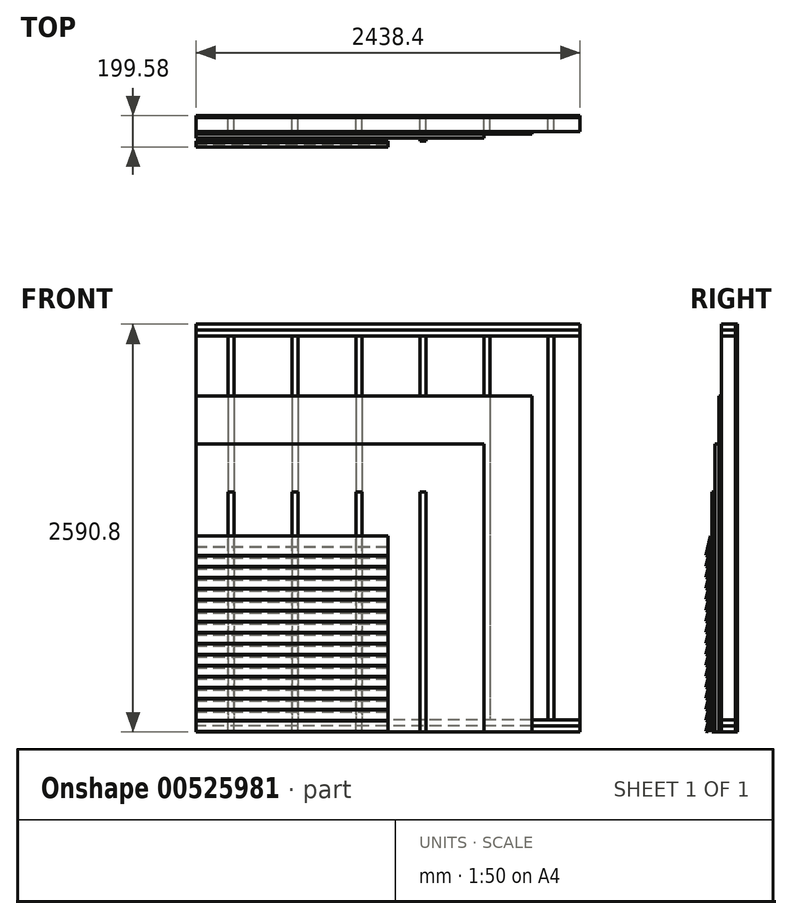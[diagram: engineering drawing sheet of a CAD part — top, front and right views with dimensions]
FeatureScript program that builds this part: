
annotation { "Feature Type Name" : "Feature", "Feature Type Description" : "" }
export const myFeature = defineFeature(function(context is Context, id is Id, definition is map)
    precondition{}
    {
        {
            var Q0;
            Q0=qCreatedBy(makeId("Right.planeOp"),FACE);
            var sketch = newSketch(context, id + "F0", { "sketchPlane" : qUnion([Q0])});
            skLineSegment(sketch, "E0.bottom", {"start": v(44.45, -1219.2) * mm, "end": v(-44.45, -1219.2) * mm});
            skLineSegment(sketch, "E0.top", {"start": v(44.45, -1257.3) * mm, "end": v(-44.45, -1257.3) * mm});
            skLineSegment(sketch, "E0.left", {"start": v(44.45, -1219.2) * mm, "end": v(44.45, -1257.3) * mm});
            skLineSegment(sketch, "E0.right", {"start": v(-44.45, -1219.2) * mm, "end": v(-44.45, -1257.3) * mm});
            skLineSegment(sketch, "E1.top", {"start": v(44.45, -1295.4) * mm, "end": v(-44.45, -1295.4) * mm});
            skLineSegment(sketch, "E1.left", {"start": v(44.45, -1257.3) * mm, "end": v(44.45, -1295.4) * mm});
            skLineSegment(sketch, "E1.right", {"start": v(-44.45, -1257.3) * mm, "end": v(-44.45, -1295.4) * mm});
            skLineSegment(sketch, "E2.bottom", {"start": v(44.45, 1295.4) * mm, "end": v(-44.45, 1295.4) * mm});
            skLineSegment(sketch, "E2.top", {"start": v(44.45, 1257.3) * mm, "end": v(-44.45, 1257.3) * mm});
            skLineSegment(sketch, "E2.left", {"start": v(44.45, 1295.4) * mm, "end": v(44.45, 1257.3) * mm});
            skLineSegment(sketch, "E2.right", {"start": v(-44.45, 1295.4) * mm, "end": v(-44.45, 1257.3) * mm});
            skLineSegment(sketch, "E3.top", {"start": v(44.45, 1219.2) * mm, "end": v(-44.45, 1219.2) * mm});
            skLineSegment(sketch, "E3.left", {"start": v(44.45, 1257.3) * mm, "end": v(44.45, 1219.2) * mm});
            skLineSegment(sketch, "E3.right", {"start": v(-44.45, 1257.3) * mm, "end": v(-44.45, 1219.2) * mm});
            skLineSegment(sketch, "E4", {"start": v(0, 0) * mm, "end": v(0, 1219.2) * mm, "construction": true});
            skLineSegment(sketch, "E5", {"start": v(0, 0) * mm, "end": v(0, -1219.2) * mm, "construction": true});
            skSolve(sketch);
        }
        {
            var Q0;
            Q0=makeQuery(id+"F0.imprint","IMPRINT",FACE,{"disambiguationData":[TD([[makeQuery(id+"F0.imprint","IMPRINT",EDGE,{"derivedFrom":sQuery(id+"F0.wireOp",EDGE,"E0.top")}),1.0]])]});
            var Q1;
            Q1=makeQuery(id+"F0.imprint","IMPRINT",FACE,{"disambiguationData":[TD([[makeQuery(id+"F0.imprint","IMPRINT",EDGE,{"derivedFrom":sQuery(id+"F0.wireOp",EDGE,"E2.bottom")}),1.0]])]});
            extrude(context, id + "F1", {"entities" : qUnion([Q0, Q1]), "endBound" : BoundingType.SYMMETRIC, "depth" : 2438.4 * mm, "offsetDistance" : 25.4 * mm});
        }
        {
            var Q0;
            Q0=makeQuery(id+"F0.imprint","IMPRINT",FACE,{"disambiguationData":[TD([[makeQuery(id+"F0.imprint","IMPRINT",EDGE,{"derivedFrom":sQuery(id+"F0.wireOp",EDGE,"E2.top")}),1.0]])]});
            var Q1;
            Q1=makeQuery(id+"F0.imprint","IMPRINT",FACE,{"disambiguationData":[TD([[makeQuery(id+"F0.imprint","IMPRINT",EDGE,{"derivedFrom":sQuery(id+"F0.wireOp",EDGE,"E0.bottom")}),1.0]])]});
            extrude(context, id + "F2", {"entities" : qUnion([Q0, Q1]), "endBound" : BoundingType.SYMMETRIC, "depth" : 2438.4 * mm, "offsetDistance" : 25.4 * mm});
        }
        {
            var Q0;
            Q0=makeQuery(id+"F2.opExtrude","SWEPT_FACE",FACE,{"disambiguationData":[OSD([sQuery(id+"F0.wireOp",EDGE,"E0.bottom")])]});
            var sketch = newSketch(context, id + "F3", { "sketchPlane" : qUnion([Q0])});
            skLineSegment(sketch, "E6.bottom", {"start": v(-1016, 44.45) * mm, "end": v(-977.9, 44.45) * mm});
            skLineSegment(sketch, "E6.top", {"start": v(-1016, -44.45) * mm, "end": v(-977.9, -44.45) * mm});
            skLineSegment(sketch, "E6.left", {"start": v(-1016, 44.45) * mm, "end": v(-1016, -44.45) * mm});
            skLineSegment(sketch, "E6.right", {"start": v(-977.9, 44.45) * mm, "end": v(-977.9, -44.45) * mm});
            skLineSegment(sketch, "E7.1.0.0", {"start": v(-609.6, 44.45) * mm, "end": v(-571.5, 44.45) * mm});
            skLineSegment(sketch, "E7.1.0.1", {"start": v(-609.6, 44.45) * mm, "end": v(-609.6, -44.45) * mm});
            skLineSegment(sketch, "E7.1.0.2", {"start": v(-571.5, 44.45) * mm, "end": v(-571.5, -44.45) * mm});
            skLineSegment(sketch, "E7.1.0.3", {"start": v(-609.6, -44.45) * mm, "end": v(-571.5, -44.45) * mm});
            skLineSegment(sketch, "E7.2.0.0", {"start": v(-203.2, 44.45) * mm, "end": v(-165.1, 44.45) * mm});
            skLineSegment(sketch, "E7.2.0.1", {"start": v(-203.2, 44.45) * mm, "end": v(-203.2, -44.45) * mm});
            skLineSegment(sketch, "E7.2.0.2", {"start": v(-165.1, 44.45) * mm, "end": v(-165.1, -44.45) * mm});
            skLineSegment(sketch, "E7.2.0.3", {"start": v(-203.2, -44.45) * mm, "end": v(-165.1, -44.45) * mm});
            skLineSegment(sketch, "E7.3.0.0", {"start": v(203.2, 44.45) * mm, "end": v(241.3, 44.45) * mm});
            skLineSegment(sketch, "E7.3.0.1", {"start": v(203.2, 44.45) * mm, "end": v(203.2, -44.45) * mm});
            skLineSegment(sketch, "E7.3.0.2", {"start": v(241.3, 44.45) * mm, "end": v(241.3, -44.45) * mm});
            skLineSegment(sketch, "E7.3.0.3", {"start": v(203.2, -44.45) * mm, "end": v(241.3, -44.45) * mm});
            skLineSegment(sketch, "E7.4.0.0", {"start": v(609.6, 44.45) * mm, "end": v(647.7, 44.45) * mm});
            skLineSegment(sketch, "E7.4.0.1", {"start": v(609.6, 44.45) * mm, "end": v(609.6, -44.45) * mm});
            skLineSegment(sketch, "E7.4.0.2", {"start": v(647.7, 44.45) * mm, "end": v(647.7, -44.45) * mm});
            skLineSegment(sketch, "E7.4.0.3", {"start": v(609.6, -44.45) * mm, "end": v(647.7, -44.45) * mm});
            skLineSegment(sketch, "E7.5.0.0", {"start": v(1016, 44.45) * mm, "end": v(1054.1, 44.45) * mm});
            skLineSegment(sketch, "E7.5.0.1", {"start": v(1016, 44.45) * mm, "end": v(1016, -44.45) * mm});
            skLineSegment(sketch, "E7.5.0.2", {"start": v(1054.1, 44.45) * mm, "end": v(1054.1, -44.45) * mm});
            skLineSegment(sketch, "E7.5.0.3", {"start": v(1016, -44.45) * mm, "end": v(1054.1, -44.45) * mm});
            skLineSegment(sketch, "E7.direction1", {"start": v(-1016, -44.45) * mm, "end": v(-609.6, -44.45) * mm, "construction": true});
            skSolve(sketch);
        }
        {
            var Q0;
            Q0 = qSketchRegion(id + "F3", true);
            var Q1;
            Q1=makeQuery(id+"F2.opExtrude","SWEPT_FACE",FACE,{"disambiguationData":[OSD([sQuery(id+"F0.wireOp",EDGE,"E3.top")])]});
            extrude(context, id + "F4", {"entities" : qUnion([Q0]), "endBound" : BoundingType.UP_TO_SURFACE, "depth" : 25.4 * mm, "endBoundEntityFace" : qUnion([Q1]), "offsetDistance" : 25.4 * mm});
        }
        {
            var Q0;
            Q0=makeQuery(id+"F1.opExtrude","CAP_FACE",FACE,{"disambiguationData":[OSD([sQuery(id+"F0.wireOp",EDGE,"E0.top"),sQuery(id+"F0.wireOp",EDGE,"E1.top"),sQuery(id+"F0.wireOp",EDGE,"E1.left"),sQuery(id+"F0.wireOp",EDGE,"E1.right")])],"isStart":true});
            var sketch = newSketch(context, id + "F5", { "sketchPlane" : qUnion([Q0])});
            skLineSegment(sketch, "E8.bottom", {"start": v(44.45, -1295.4) * mm, "end": v(60.32, -1295.4) * mm});
            skLineSegment(sketch, "E8.top", {"start": v(44.45, 838.2) * mm, "end": v(60.32, 838.2) * mm});
            skLineSegment(sketch, "E8.left", {"start": v(44.45, -1295.4) * mm, "end": v(44.45, 838.2) * mm});
            skLineSegment(sketch, "E8.right", {"start": v(60.32, -1295.4) * mm, "end": v(60.32, 838.2) * mm});
            skLineSegment(sketch, "E9.0.0", {"start": v(-44.45, 1257.3) * mm, "end": v(44.45, 1257.3) * mm});
            skLineSegment(sketch, "E9.0.1", {"start": v(44.45, 1257.3) * mm, "end": v(44.45, 1295.4) * mm});
            skLineSegment(sketch, "E9.0.2", {"start": v(44.45, 1295.4) * mm, "end": v(-44.45, 1295.4) * mm});
            skLineSegment(sketch, "E9.0.3", {"start": v(-44.45, 1295.4) * mm, "end": v(-44.45, 1257.3) * mm});
            skLineSegment(sketch, "E10.bottom", {"start": v(-44.45, 1295.4) * mm, "end": v(-57.15, 1295.4) * mm});
            skLineSegment(sketch, "E10.top", {"start": v(-44.45, -1295.4) * mm, "end": v(-57.15, -1295.4) * mm});
            skLineSegment(sketch, "E10.left", {"start": v(-44.45, 1295.4) * mm, "end": v(-44.45, -1295.4) * mm});
            skLineSegment(sketch, "E10.right", {"start": v(-57.15, 1295.4) * mm, "end": v(-57.15, -1295.4) * mm});
            skLineSegment(sketch, "E11.bottom", {"start": v(60.32, -1295.4) * mm, "end": v(85.72, -1295.4) * mm});
            skLineSegment(sketch, "E11.top", {"start": v(60.32, 533.4) * mm, "end": v(85.72, 533.4) * mm});
            skLineSegment(sketch, "E11.left", {"start": v(60.32, -1295.4) * mm, "end": v(60.32, 533.4) * mm});
            skLineSegment(sketch, "E11.right", {"start": v(85.72, -1295.4) * mm, "end": v(85.72, 533.4) * mm});
            skSolve(sketch);
        }
        {
            var Q0;
            {var subQ3=sQuery(id+"F5.wireOp",EDGE,"E10.bottom");Q0=makeQuery(id+"F5.imprint","IMPRINT",FACE,{"disambiguationData":[TD([[makeQuery(id+"F5.imprint","IMPRINT",EDGE,{"derivedFrom":subQ3}),1.0]])]});}
            var Q1;
            Q1=makeQuery(id+"F2.opExtrude","CAP_FACE",FACE,{"disambiguationData":[OSD([sQuery(id+"F0.wireOp",EDGE,"E2.top"),sQuery(id+"F0.wireOp",EDGE,"E3.top"),sQuery(id+"F0.wireOp",EDGE,"E3.left"),sQuery(id+"F0.wireOp",EDGE,"E3.right")])],"isStart":false});
            extrude(context, id + "F6", {"entities" : qUnion([Q0]), "endBound" : BoundingType.UP_TO_SURFACE, "oppositeDirection" : true, "depth" : 25.4 * mm, "endBoundEntityFace" : qUnion([Q1]), "offsetDistance" : 25.4 * mm});
        }
        {
            var Q0;
            {var subQ2=sQuery(id+"F5.wireOp",EDGE,"E8.bottom");Q0=makeQuery(id+"F5.imprint","IMPRINT",FACE,{"disambiguationData":[TD([[makeQuery(id+"F5.imprint","IMPRINT",EDGE,{"derivedFrom":subQ2}),1.0]])]});}
            extrude(context, id + "F7", {"entities" : qUnion([Q0]), "oppositeDirection" : true, "depth" : 2133.6 * mm, "offsetDistance" : 25.4 * mm});
        }
        {
            var Q0;
            Q0=makeQuery(id+"F5.imprint","IMPRINT",FACE,{"disambiguationData":[TD([[makeQuery(id+"F5.imprint","IMPRINT",EDGE,{"derivedFrom":sQuery(id+"F5.wireOp",EDGE,"E11.bottom")}),1.0]])]});
            extrude(context, id + "F8", {"entities" : qUnion([Q0]), "oppositeDirection" : true, "depth" : 1828.8 * mm, "offsetDistance" : 25.4 * mm});
        }
        {
            var Q0;
            Q0=makeQuery(id+"F8.opExtrude","SWEPT_FACE",FACE,{"disambiguationData":[OSD([sQuery(id+"F5.wireOp",EDGE,"E11.right")])]});
            var sketch = newSketch(context, id + "F9", { "sketchPlane" : qUnion([Q0])});
            skLineSegment(sketch, "E12.0.0", {"start": v(-977.9, 1219.2) * mm, "end": v(-1016, 1219.2) * mm});
            skLineSegment(sketch, "E12.0.1", {"start": v(-1016, 1219.2) * mm, "end": v(-1016, -1219.2) * mm});
            skLineSegment(sketch, "E12.0.2", {"start": v(-1016, -1219.2) * mm, "end": v(-977.9, -1219.2) * mm});
            skLineSegment(sketch, "E12.0.3", {"start": v(-977.9, -1219.2) * mm, "end": v(-977.9, 1219.2) * mm});
            skLineSegment(sketch, "E13.bottom", {"start": v(-1016, -1295.4) * mm, "end": v(-977.9, -1295.4) * mm});
            skLineSegment(sketch, "E13.top", {"start": v(-1016, 228.6) * mm, "end": v(-977.9, 228.6) * mm});
            skLineSegment(sketch, "E13.left", {"start": v(-1016, -1295.4) * mm, "end": v(-1016, 228.6) * mm});
            skLineSegment(sketch, "E13.right", {"start": v(-977.9, -1295.4) * mm, "end": v(-977.9, 228.6) * mm});
            skLineSegment(sketch, "E14.1.0.0", {"start": v(-571.5, -1295.4) * mm, "end": v(-571.5, 228.6) * mm});
            skLineSegment(sketch, "E14.1.0.1", {"start": v(-609.6, 228.6) * mm, "end": v(-571.5, 228.6) * mm});
            skLineSegment(sketch, "E14.1.0.2", {"start": v(-609.6, -1295.4) * mm, "end": v(-571.5, -1295.4) * mm});
            skLineSegment(sketch, "E14.1.0.3", {"start": v(-609.6, -1295.4) * mm, "end": v(-609.6, 228.6) * mm});
            skLineSegment(sketch, "E14.2.0.0", {"start": v(-165.1, -1295.4) * mm, "end": v(-165.1, 228.6) * mm});
            skLineSegment(sketch, "E14.2.0.1", {"start": v(-203.2, 228.6) * mm, "end": v(-165.1, 228.6) * mm});
            skLineSegment(sketch, "E14.2.0.2", {"start": v(-203.2, -1295.4) * mm, "end": v(-165.1, -1295.4) * mm});
            skLineSegment(sketch, "E14.2.0.3", {"start": v(-203.2, -1295.4) * mm, "end": v(-203.2, 228.6) * mm});
            skLineSegment(sketch, "E14.3.0.0", {"start": v(241.3, -1295.4) * mm, "end": v(241.3, 228.6) * mm});
            skLineSegment(sketch, "E14.3.0.1", {"start": v(203.2, 228.6) * mm, "end": v(241.3, 228.6) * mm});
            skLineSegment(sketch, "E14.3.0.2", {"start": v(203.2, -1295.4) * mm, "end": v(241.3, -1295.4) * mm});
            skLineSegment(sketch, "E14.3.0.3", {"start": v(203.2, -1295.4) * mm, "end": v(203.2, 228.6) * mm});
            skLineSegment(sketch, "E14.direction1", {"start": v(-1016, -1295.4) * mm, "end": v(-609.6, -1295.4) * mm, "construction": true});
            skSolve(sketch);
        }
        {
            var Q0;
            Q0=makeQuery(id+"F9.imprint","IMPRINT",FACE,{"disambiguationData":[TD([[makeQuery(id+"F9.imprint","IMPRINT",EDGE,{"derivedFrom":sQuery(id+"F9.wireOp",EDGE,"E14.1.0.0")}),1.0]])]});
            var Q1;
            Q1=makeQuery(id+"F9.imprint","IMPRINT",FACE,{"disambiguationData":[TD([[makeQuery(id+"F9.imprint","IMPRINT",EDGE,{"derivedFrom":sQuery(id+"F9.wireOp",EDGE,"E14.2.0.0")}),1.0]])]});
            var Q2;
            Q2=makeQuery(id+"F9.imprint","IMPRINT",FACE,{"disambiguationData":[TD([[makeQuery(id+"F9.imprint","IMPRINT",EDGE,{"derivedFrom":sQuery(id+"F9.wireOp",EDGE,"E14.3.0.0")}),1.0]])]});
            var Q3;
            {var subQ0=sQuery(id+"F9.wireOp",EDGE,"E12.0.2");Q3=makeQuery(id+"F9.imprint","IMPRINT",FACE,{"disambiguationData":[TD([[makeQuery(id+"F9.imprint","IMPRINT",EDGE,{"derivedFrom":subQ0}),-1.0]])]});}
            var Q4;
            {var subQ0=sQuery(id+"F9.wireOp",EDGE,"E12.0.2");Q4=makeQuery(id+"F9.imprint","IMPRINT",FACE,{"disambiguationData":[TD([[makeQuery(id+"F9.imprint","IMPRINT",EDGE,{"derivedFrom":subQ0}),1.0]])]});}
            extrude(context, id + "F10", {"entities" : qUnion([Q0, Q1, Q2, Q3, Q4]), "depth" : 19.05 * mm, "offsetDistance" : 25.4 * mm});
        }
        {
            var Q0;
            Q0=makeQuery(id+"F8.opExtrude","CAP_FACE",FACE,{"disambiguationData":[OSD([sQuery(id+"F5.wireOp",EDGE,"E11.bottom"),sQuery(id+"F5.wireOp",EDGE,"E11.top"),sQuery(id+"F5.wireOp",EDGE,"E11.left"),sQuery(id+"F5.wireOp",EDGE,"E11.right")])],"isStart":true});
            var sketch = newSketch(context, id + "F11", { "sketchPlane" : qUnion([Q0])});
            skLineSegment(sketch, "E15.0.0", {"start": v(85.72, 228.6) * mm, "end": v(85.72, -1295.4) * mm});
            skLineSegment(sketch, "E15.0.1", {"start": v(85.72, -1295.4) * mm, "end": v(104.77, -1295.4) * mm});
            skLineSegment(sketch, "E15.0.2", {"start": v(104.77, -1295.4) * mm, "end": v(104.77, 228.6) * mm});
            skLineSegment(sketch, "E15.0.3", {"start": v(104.77, 228.6) * mm, "end": v(85.72, 228.6) * mm});
            skLineSegment(sketch, "E16", {"start": v(104.77, -1170.49) * mm, "end": v(126.8, -1295.4) * mm});
            skLineSegment(sketch, "E17", {"start": v(126.8, -1295.4) * mm, "end": v(142.43, -1292.64) * mm});
            skLineSegment(sketch, "E18", {"start": v(142.43, -1292.64) * mm, "end": v(114.16, -1168.83) * mm});
            skLineSegment(sketch, "E19", {"start": v(114.16, -1168.83) * mm, "end": v(104.77, -1170.49) * mm});
            skLineSegment(sketch, "E20.0.1.0", {"start": v(142.43, -1222.8) * mm, "end": v(114.16, -1098.98) * mm});
            skLineSegment(sketch, "E20.0.1.1", {"start": v(126.8, -1225.55) * mm, "end": v(142.43, -1222.8) * mm});
            skLineSegment(sketch, "E20.0.1.2", {"start": v(104.77, -1100.64) * mm, "end": v(126.8, -1225.55) * mm});
            skLineSegment(sketch, "E20.0.1.3", {"start": v(114.16, -1098.98) * mm, "end": v(104.77, -1100.64) * mm});
            skLineSegment(sketch, "E20.0.2.0", {"start": v(142.43, -1152.94) * mm, "end": v(114.16, -1029.13) * mm});
            skLineSegment(sketch, "E20.0.2.1", {"start": v(126.8, -1155.7) * mm, "end": v(142.43, -1152.94) * mm});
            skLineSegment(sketch, "E20.0.2.2", {"start": v(104.77, -1030.79) * mm, "end": v(126.8, -1155.7) * mm});
            skLineSegment(sketch, "E20.0.2.3", {"start": v(114.16, -1029.13) * mm, "end": v(104.77, -1030.79) * mm});
            skLineSegment(sketch, "E20.0.3.0", {"start": v(142.43, -1083.1) * mm, "end": v(114.16, -959.28) * mm});
            skLineSegment(sketch, "E20.0.3.1", {"start": v(126.8, -1085.85) * mm, "end": v(142.43, -1083.1) * mm});
            skLineSegment(sketch, "E20.0.3.2", {"start": v(104.77, -960.94) * mm, "end": v(126.8, -1085.85) * mm});
            skLineSegment(sketch, "E20.0.3.3", {"start": v(114.16, -959.28) * mm, "end": v(104.77, -960.94) * mm});
            skLineSegment(sketch, "E20.0.4.0", {"start": v(142.43, -1013.24) * mm, "end": v(114.16, -889.43) * mm});
            skLineSegment(sketch, "E20.0.4.1", {"start": v(126.8, -1016) * mm, "end": v(142.43, -1013.24) * mm});
            skLineSegment(sketch, "E20.0.4.2", {"start": v(104.77, -891.09) * mm, "end": v(126.8, -1016) * mm});
            skLineSegment(sketch, "E20.0.4.3", {"start": v(114.16, -889.43) * mm, "end": v(104.77, -891.09) * mm});
            skLineSegment(sketch, "E20.0.5.0", {"start": v(142.43, -943.4) * mm, "end": v(114.16, -819.58) * mm});
            skLineSegment(sketch, "E20.0.5.1", {"start": v(126.8, -946.15) * mm, "end": v(142.43, -943.4) * mm});
            skLineSegment(sketch, "E20.0.5.2", {"start": v(104.77, -821.24) * mm, "end": v(126.8, -946.15) * mm});
            skLineSegment(sketch, "E20.0.5.3", {"start": v(114.16, -819.58) * mm, "end": v(104.77, -821.24) * mm});
            skLineSegment(sketch, "E20.0.6.0", {"start": v(142.43, -873.54) * mm, "end": v(114.16, -749.73) * mm});
            skLineSegment(sketch, "E20.0.6.1", {"start": v(126.8, -876.3) * mm, "end": v(142.43, -873.54) * mm});
            skLineSegment(sketch, "E20.0.6.2", {"start": v(104.77, -751.39) * mm, "end": v(126.8, -876.3) * mm});
            skLineSegment(sketch, "E20.0.6.3", {"start": v(114.16, -749.73) * mm, "end": v(104.77, -751.39) * mm});
            skLineSegment(sketch, "E20.0.7.0", {"start": v(142.43, -803.7) * mm, "end": v(114.16, -679.88) * mm});
            skLineSegment(sketch, "E20.0.7.1", {"start": v(126.8, -806.45) * mm, "end": v(142.43, -803.7) * mm});
            skLineSegment(sketch, "E20.0.7.2", {"start": v(104.77, -681.54) * mm, "end": v(126.8, -806.45) * mm});
            skLineSegment(sketch, "E20.0.7.3", {"start": v(114.16, -679.88) * mm, "end": v(104.77, -681.54) * mm});
            skLineSegment(sketch, "E20.0.8.0", {"start": v(142.43, -733.84) * mm, "end": v(114.16, -610.03) * mm});
            skLineSegment(sketch, "E20.0.8.1", {"start": v(126.8, -736.6) * mm, "end": v(142.43, -733.84) * mm});
            skLineSegment(sketch, "E20.0.8.2", {"start": v(104.77, -611.69) * mm, "end": v(126.8, -736.6) * mm});
            skLineSegment(sketch, "E20.0.8.3", {"start": v(114.16, -610.03) * mm, "end": v(104.77, -611.69) * mm});
            skLineSegment(sketch, "E20.0.9.0", {"start": v(142.43, -664) * mm, "end": v(114.16, -540.18) * mm});
            skLineSegment(sketch, "E20.0.9.1", {"start": v(126.8, -666.75) * mm, "end": v(142.43, -664) * mm});
            skLineSegment(sketch, "E20.0.9.2", {"start": v(104.77, -541.84) * mm, "end": v(126.8, -666.75) * mm});
            skLineSegment(sketch, "E20.0.9.3", {"start": v(114.16, -540.18) * mm, "end": v(104.77, -541.84) * mm});
            skLineSegment(sketch, "E20.0.10.0", {"start": v(142.43, -594.14) * mm, "end": v(114.16, -470.33) * mm});
            skLineSegment(sketch, "E20.0.10.1", {"start": v(126.8, -596.9) * mm, "end": v(142.43, -594.14) * mm});
            skLineSegment(sketch, "E20.0.10.2", {"start": v(104.77, -471.99) * mm, "end": v(126.8, -596.9) * mm});
            skLineSegment(sketch, "E20.0.10.3", {"start": v(114.16, -470.33) * mm, "end": v(104.77, -471.99) * mm});
            skLineSegment(sketch, "E20.0.11.0", {"start": v(142.43, -524.3) * mm, "end": v(114.16, -400.48) * mm});
            skLineSegment(sketch, "E20.0.11.1", {"start": v(126.8, -527.05) * mm, "end": v(142.43, -524.3) * mm});
            skLineSegment(sketch, "E20.0.11.2", {"start": v(104.77, -402.14) * mm, "end": v(126.8, -527.05) * mm});
            skLineSegment(sketch, "E20.0.11.3", {"start": v(114.16, -400.48) * mm, "end": v(104.77, -402.14) * mm});
            skLineSegment(sketch, "E20.0.12.0", {"start": v(142.43, -454.44) * mm, "end": v(114.16, -330.63) * mm});
            skLineSegment(sketch, "E20.0.12.1", {"start": v(126.8, -457.2) * mm, "end": v(142.43, -454.44) * mm});
            skLineSegment(sketch, "E20.0.12.2", {"start": v(104.77, -332.29) * mm, "end": v(126.8, -457.2) * mm});
            skLineSegment(sketch, "E20.0.12.3", {"start": v(114.16, -330.63) * mm, "end": v(104.77, -332.29) * mm});
            skLineSegment(sketch, "E20.0.13.0", {"start": v(142.43, -384.6) * mm, "end": v(114.16, -260.78) * mm});
            skLineSegment(sketch, "E20.0.13.1", {"start": v(126.8, -387.35) * mm, "end": v(142.43, -384.6) * mm});
            skLineSegment(sketch, "E20.0.13.2", {"start": v(104.77, -262.44) * mm, "end": v(126.8, -387.35) * mm});
            skLineSegment(sketch, "E20.0.13.3", {"start": v(114.16, -260.78) * mm, "end": v(104.77, -262.44) * mm});
            skLineSegment(sketch, "E20.0.14.0", {"start": v(142.43, -314.74) * mm, "end": v(114.16, -190.93) * mm});
            skLineSegment(sketch, "E20.0.14.1", {"start": v(126.8, -317.5) * mm, "end": v(142.43, -314.74) * mm});
            skLineSegment(sketch, "E20.0.14.2", {"start": v(104.77, -192.59) * mm, "end": v(126.8, -317.5) * mm});
            skLineSegment(sketch, "E20.0.14.3", {"start": v(114.16, -190.93) * mm, "end": v(104.77, -192.59) * mm});
            skLineSegment(sketch, "E20.0.15.0", {"start": v(142.43, -244.9) * mm, "end": v(114.16, -121.08) * mm});
            skLineSegment(sketch, "E20.0.15.1", {"start": v(126.8, -247.65) * mm, "end": v(142.43, -244.9) * mm});
            skLineSegment(sketch, "E20.0.15.2", {"start": v(104.77, -122.74) * mm, "end": v(126.8, -247.65) * mm});
            skLineSegment(sketch, "E20.0.15.3", {"start": v(114.16, -121.08) * mm, "end": v(104.77, -122.74) * mm});
            skLineSegment(sketch, "E20.0.16.0", {"start": v(142.43, -175.04) * mm, "end": v(114.16, -51.23) * mm});
            skLineSegment(sketch, "E20.0.16.1", {"start": v(126.8, -177.8) * mm, "end": v(142.43, -175.04) * mm});
            skLineSegment(sketch, "E20.0.16.2", {"start": v(104.77, -52.89) * mm, "end": v(126.8, -177.8) * mm});
            skLineSegment(sketch, "E20.0.16.3", {"start": v(114.16, -51.23) * mm, "end": v(104.77, -52.89) * mm});
            skLineSegment(sketch, "E20.direction1", {"start": v(126.8, -1295.4) * mm, "end": v(195.46, -1295.4) * mm, "construction": true});
            skLineSegment(sketch, "E20.direction2", {"start": v(126.8, -1295.4) * mm, "end": v(126.8, -1225.55) * mm, "construction": true});
            skLineSegment(sketch, "E21", {"start": v(104.77, -1295.4) * mm, "end": v(126.8, -1295.4) * mm, "construction": true});
            skSolve(sketch);
        }
        {
            var Q0;
            Q0=makeQuery(id+"F11.imprint","IMPRINT",FACE,{"disambiguationData":[TD([[makeQuery(id+"F11.imprint","IMPRINT",EDGE,{"derivedFrom":sQuery(id+"F11.wireOp",EDGE,"E16")}),1.0]])]});
            var Q1;
            Q1=makeQuery(id+"F11.imprint","IMPRINT",FACE,{"disambiguationData":[TD([[makeQuery(id+"F11.imprint","IMPRINT",EDGE,{"derivedFrom":sQuery(id+"F11.wireOp",EDGE,"E20.0.1.0")}),1.0]])]});
            var Q2;
            Q2=makeQuery(id+"F11.imprint","IMPRINT",FACE,{"disambiguationData":[TD([[makeQuery(id+"F11.imprint","IMPRINT",EDGE,{"derivedFrom":sQuery(id+"F11.wireOp",EDGE,"E20.0.2.0")}),1.0]])]});
            var Q3;
            Q3=makeQuery(id+"F11.imprint","IMPRINT",FACE,{"disambiguationData":[TD([[makeQuery(id+"F11.imprint","IMPRINT",EDGE,{"derivedFrom":sQuery(id+"F11.wireOp",EDGE,"E20.0.3.0")}),1.0]])]});
            var Q4;
            Q4=makeQuery(id+"F11.imprint","IMPRINT",FACE,{"disambiguationData":[TD([[makeQuery(id+"F11.imprint","IMPRINT",EDGE,{"derivedFrom":sQuery(id+"F11.wireOp",EDGE,"E20.0.4.0")}),1.0]])]});
            var Q5;
            Q5=makeQuery(id+"F11.imprint","IMPRINT",FACE,{"disambiguationData":[TD([[makeQuery(id+"F11.imprint","IMPRINT",EDGE,{"derivedFrom":sQuery(id+"F11.wireOp",EDGE,"E20.0.5.0")}),1.0]])]});
            var Q6;
            Q6=makeQuery(id+"F11.imprint","IMPRINT",FACE,{"disambiguationData":[TD([[makeQuery(id+"F11.imprint","IMPRINT",EDGE,{"derivedFrom":sQuery(id+"F11.wireOp",EDGE,"E20.0.6.0")}),1.0]])]});
            var Q7;
            Q7=makeQuery(id+"F11.imprint","IMPRINT",FACE,{"disambiguationData":[TD([[makeQuery(id+"F11.imprint","IMPRINT",EDGE,{"derivedFrom":sQuery(id+"F11.wireOp",EDGE,"E20.0.7.0")}),1.0]])]});
            var Q8;
            Q8=makeQuery(id+"F11.imprint","IMPRINT",FACE,{"disambiguationData":[TD([[makeQuery(id+"F11.imprint","IMPRINT",EDGE,{"derivedFrom":sQuery(id+"F11.wireOp",EDGE,"E20.0.8.0")}),1.0]])]});
            var Q9;
            Q9=makeQuery(id+"F11.imprint","IMPRINT",FACE,{"disambiguationData":[TD([[makeQuery(id+"F11.imprint","IMPRINT",EDGE,{"derivedFrom":sQuery(id+"F11.wireOp",EDGE,"E20.0.9.0")}),1.0]])]});
            var Q10;
            Q10=makeQuery(id+"F11.imprint","IMPRINT",FACE,{"disambiguationData":[TD([[makeQuery(id+"F11.imprint","IMPRINT",EDGE,{"derivedFrom":sQuery(id+"F11.wireOp",EDGE,"E20.0.10.0")}),1.0]])]});
            var Q11;
            Q11=makeQuery(id+"F11.imprint","IMPRINT",FACE,{"disambiguationData":[TD([[makeQuery(id+"F11.imprint","IMPRINT",EDGE,{"derivedFrom":sQuery(id+"F11.wireOp",EDGE,"E20.0.11.0")}),1.0]])]});
            var Q12;
            Q12=makeQuery(id+"F11.imprint","IMPRINT",FACE,{"disambiguationData":[TD([[makeQuery(id+"F11.imprint","IMPRINT",EDGE,{"derivedFrom":sQuery(id+"F11.wireOp",EDGE,"E20.0.12.0")}),1.0]])]});
            var Q13;
            Q13=makeQuery(id+"F11.imprint","IMPRINT",FACE,{"disambiguationData":[TD([[makeQuery(id+"F11.imprint","IMPRINT",EDGE,{"derivedFrom":sQuery(id+"F11.wireOp",EDGE,"E20.0.13.0")}),1.0]])]});
            var Q14;
            Q14=makeQuery(id+"F11.imprint","IMPRINT",FACE,{"disambiguationData":[TD([[makeQuery(id+"F11.imprint","IMPRINT",EDGE,{"derivedFrom":sQuery(id+"F11.wireOp",EDGE,"E20.0.14.0")}),1.0]])]});
            var Q15;
            Q15=makeQuery(id+"F11.imprint","IMPRINT",FACE,{"disambiguationData":[TD([[makeQuery(id+"F11.imprint","IMPRINT",EDGE,{"derivedFrom":sQuery(id+"F11.wireOp",EDGE,"E20.0.15.0")}),1.0]])]});
            var Q16;
            Q16=makeQuery(id+"F11.imprint","IMPRINT",FACE,{"disambiguationData":[TD([[makeQuery(id+"F11.imprint","IMPRINT",EDGE,{"derivedFrom":sQuery(id+"F11.wireOp",EDGE,"E20.0.16.0")}),1.0]])]});
            extrude(context, id + "F12", {"entities" : qUnion([Q0, Q1, Q2, Q3, Q4, Q5, Q6, Q7, Q8, Q9, Q10, Q11, Q12, Q13, Q14, Q15, Q16]), "oppositeDirection" : true, "depth" : 1219.2 * mm, "offsetDistance" : 25.4 * mm});
        }
    });
